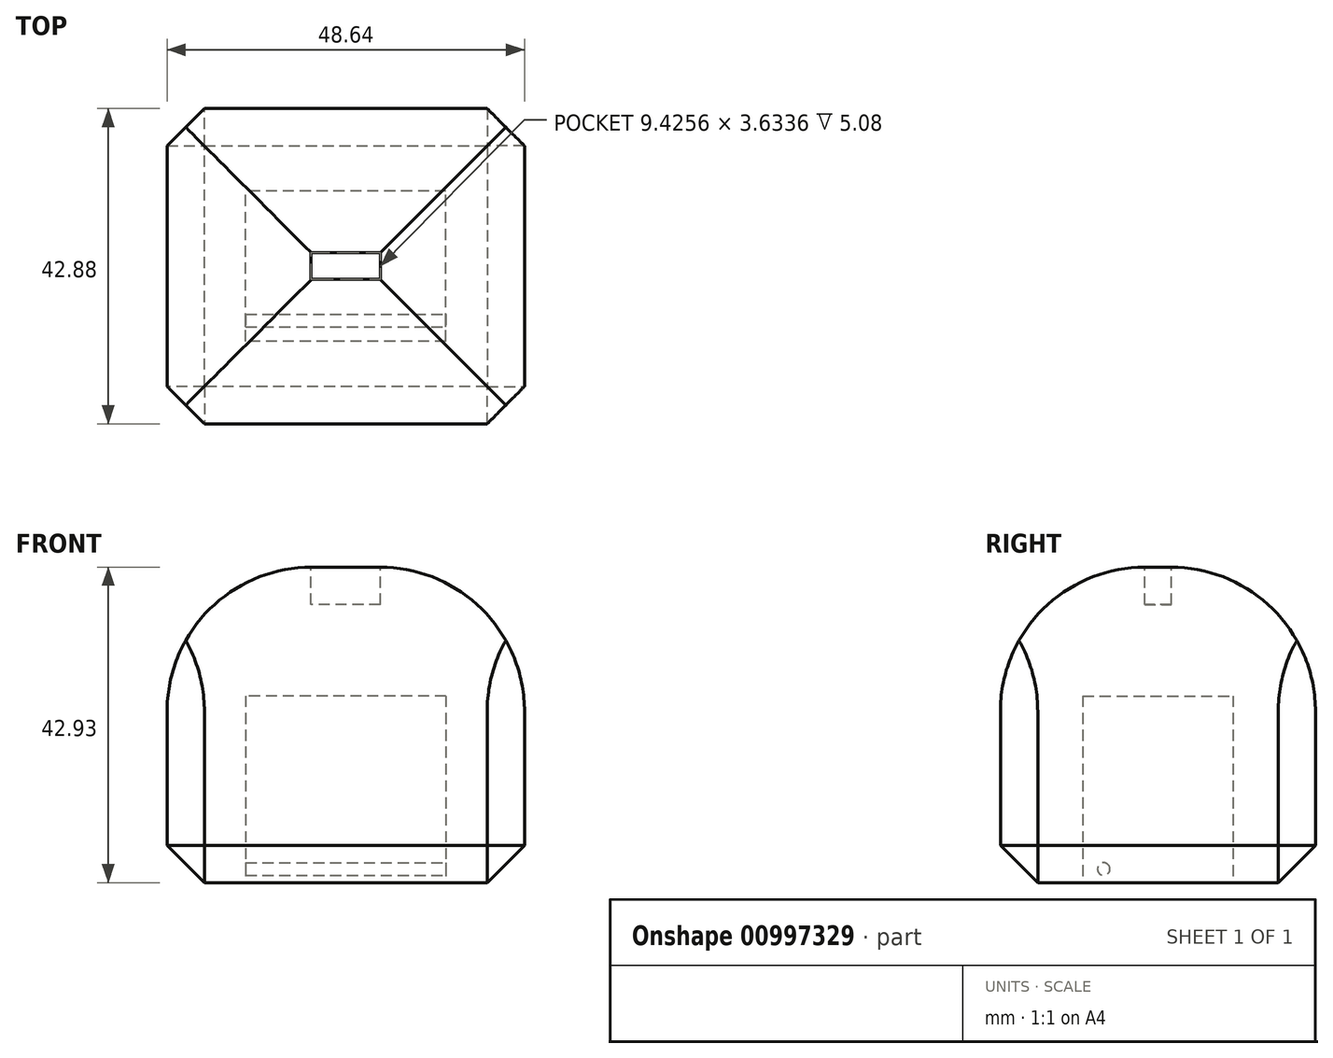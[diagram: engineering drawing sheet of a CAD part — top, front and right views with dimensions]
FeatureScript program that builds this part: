
annotation { "Feature Type Name" : "Feature", "Feature Type Description" : "" }
export const myFeature = defineFeature(function(context is Context, id is Id, definition is map)
    precondition{}
    {
        {
            var Q0;
            Q0=qCreatedBy(makeId("Top.planeOp"),FACE);
            var sketch = newSketch(context, id + "F0", { "sketchPlane" : qUnion([Q0])});
            skLineSegment(sketch, "E0.bottom", {"start": v(24.32, 21.44) * mm, "end": v(-24.32, 21.44) * mm});
            skLineSegment(sketch, "E0.top", {"start": v(24.32, -21.44) * mm, "end": v(-24.32, -21.44) * mm});
            skLineSegment(sketch, "E0.left", {"start": v(24.32, 21.44) * mm, "end": v(24.32, -21.44) * mm});
            skLineSegment(sketch, "E0.right", {"start": v(-24.32, 21.44) * mm, "end": v(-24.32, -21.44) * mm});
            skPoint(sketch, "E0.middle", {"position": v(0, 0) * mm});
            skSolve(sketch);
        }
        {
            var Q0;
            Q0=qSketchRegion(id+"F0",true);
            extrude(context, id + "F1", {"entities" : qUnion([Q0]), "depth" : 42.93 * mm, "offsetDistance" : 25.4 * mm});
        }
        {
            var Q0;
            Q0=makeQuery(id+"F1.opExtrude","CAP_EDGE",EDGE,{"disambiguationData":[OSD([sQuery(id+"F0.wireOp",EDGE,"E0.left")])],"isStart":false});
            var Q1;
            Q1=makeQuery(id+"F1.opExtrude","CAP_EDGE",EDGE,{"disambiguationData":[OSD([sQuery(id+"F0.wireOp",EDGE,"E0.top")])],"isStart":false});
            var Q2;
            Q2=makeQuery(id+"F1.opExtrude","CAP_EDGE",EDGE,{"disambiguationData":[OSD([sQuery(id+"F0.wireOp",EDGE,"E0.bottom")])],"isStart":false});
            var Q3;
            Q3=makeQuery(id+"F1.opExtrude","CAP_EDGE",EDGE,{"disambiguationData":[OSD([sQuery(id+"F0.wireOp",EDGE,"E0.right")])],"isStart":false});
            fillet(context, id + "F2", {"entities" : qUnion([Q0, Q1, Q2, Q3]), "radius" : 19.62 * mm, "tangentPropagation" : true, "allowEdgeOverflow" : false});
        }
        {
            var Q0;
            Q0=makeQuery(id+"F1.opExtrude","CAP_FACE",FACE,{"disambiguationData":[OSD([sQuery(id+"F0.wireOp",EDGE,"E0.bottom"),sQuery(id+"F0.wireOp",EDGE,"E0.top"),sQuery(id+"F0.wireOp",EDGE,"E0.left"),sQuery(id+"F0.wireOp",EDGE,"E0.right")])],"isStart":false});
            cPlane(context, id + "F3", {"entities" : qUnion([Q0]), "cplaneType" : CPlaneType.OFFSET, "offset" : 0 * mm, "width" : 152.4 * mm, "height" : 152.4 * mm});
        }
        {
            var Q0;
            Q0=qCreatedBy(id+"F3.planeOp",FACE);
            var sketch = newSketch(context, id + "F4", { "sketchPlane" : qUnion([Q0])});
            skLineSegment(sketch, "E1", {"start": v(-4.71, 1.83) * mm, "end": v(-4.71, -1.8) * mm});
            skLineSegment(sketch, "E2", {"start": v(-4.71, -1.8) * mm, "end": v(4.71, -1.8) * mm});
            skLineSegment(sketch, "E3", {"start": v(4.71, -1.8) * mm, "end": v(4.71, 1.82) * mm});
            skLineSegment(sketch, "E4", {"start": v(4.71, 1.82) * mm, "end": v(-4.71, 1.83) * mm});
            skSolve(sketch);
        }
        {
            var Q0;
            Q0=makeQuery(id+"F4.imprint","IMPRINT",FACE,{"disambiguationData":[TD([[makeQuery(id+"F4.imprint","IMPRINT",EDGE,{"derivedFrom":sQuery(id+"F4.wireOp",EDGE,"E1")}),1.0]])]});
            extrude(context, id + "F5", {"entities" : qUnion([Q0]), "operationType" : NewBodyOperationType.REMOVE, "oppositeDirection" : true, "depth" : 5.08 * mm, "offsetDistance" : 25.4 * mm});
        }
        {
            var Q0;
            Q0=makeQuery(id+"F1.opExtrude","CAP_FACE",FACE,{"disambiguationData":[OSD([sQuery(id+"F0.wireOp",EDGE,"E0.bottom"),sQuery(id+"F0.wireOp",EDGE,"E0.top"),sQuery(id+"F0.wireOp",EDGE,"E0.left"),sQuery(id+"F0.wireOp",EDGE,"E0.right")])],"isStart":true});
            var Q1;
            Q1=makeQuery(id+"F1.opExtrude","SWEPT_FACE",FACE,{"disambiguationData":[OSD([sQuery(id+"F0.wireOp",EDGE,"E0.right")])]});
            var Q2;
            Q2=makeQuery(id+"F1.opExtrude","SWEPT_FACE",FACE,{"disambiguationData":[OSD([sQuery(id+"F0.wireOp",EDGE,"E0.top")])]});
            var Q3;
            Q3=makeQuery(id+"F1.opExtrude","SWEPT_FACE",FACE,{"disambiguationData":[OSD([sQuery(id+"F0.wireOp",EDGE,"E0.left")])]});
            var Q4;
            Q4=makeQuery(id+"F1.opExtrude","SWEPT_FACE",FACE,{"disambiguationData":[OSD([sQuery(id+"F0.wireOp",EDGE,"E0.bottom")])]});
            chamfer(context, id + "F6", {"entities" : qUnion([Q0, Q1, Q2, Q3, Q4]), "width" : 5.08 * mm, "tangentPropagation" : true});
        }
        {
            var Q0;
            Q0=makeQuery(id+"F1.opExtrude","CAP_FACE",FACE,{"disambiguationData":[OSD([sQuery(id+"F0.wireOp",EDGE,"E0.bottom"),sQuery(id+"F0.wireOp",EDGE,"E0.top"),sQuery(id+"F0.wireOp",EDGE,"E0.left"),sQuery(id+"F0.wireOp",EDGE,"E0.right")])],"isStart":true});
            var sketch = newSketch(context, id + "F7", { "sketchPlane" : qUnion([Q0])});
            skLineSegment(sketch, "E5.bottom", {"start": v(13.63, 10.22) * mm, "end": v(-13.63, 10.22) * mm});
            skLineSegment(sketch, "E5.top", {"start": v(13.63, -10.22) * mm, "end": v(-13.63, -10.22) * mm});
            skLineSegment(sketch, "E5.left", {"start": v(13.63, 10.22) * mm, "end": v(13.63, -10.22) * mm});
            skLineSegment(sketch, "E5.right", {"start": v(-13.63, 10.22) * mm, "end": v(-13.63, -10.22) * mm});
            skPoint(sketch, "E5.middle", {"position": v(0, 0) * mm});
            skSolve(sketch);
        }
        {
            var Q0;
            Q0=makeQuery(id+"F7.imprint","IMPRINT",FACE,{"disambiguationData":[TD([[makeQuery(id+"F7.imprint","IMPRINT",EDGE,{"derivedFrom":sQuery(id+"F7.wireOp",EDGE,"E5.bottom")}),1.0]])]});
            extrude(context, id + "F8", {"entities" : qUnion([Q0]), "operationType" : NewBodyOperationType.REMOVE, "oppositeDirection" : true, "depth" : 25.4 * mm, "offsetDistance" : 25.4 * mm});
        }
        {
            var Q0;
            Q0=makeQuery(id+"F8.boolean.opBoolean","COPY",FACE,{"derivedFrom":makeQuery(id+"F8.opExtrude","SWEPT_FACE",FACE,{"disambiguationData":[OSD([sQuery(id+"F7.wireOp",EDGE,"E5.left")])]})});
            var sketch = newSketch(context, id + "F9", { "sketchPlane" : qUnion([Q0])});
            skCircle(sketch, "E6", {"center": v(7.38, 1.85) * mm, "radius": 0.85 * mm});
            skSolve(sketch);
        }
        {
            var Q0;
            Q0=qSketchRegion(id+"F9",true);
            extrude(context, id + "F10", {"entities" : qUnion([Q0]), "operationType" : NewBodyOperationType.ADD, "depth" : 27.48 * mm, "offsetDistance" : 25.4 * mm});
        }
    });
